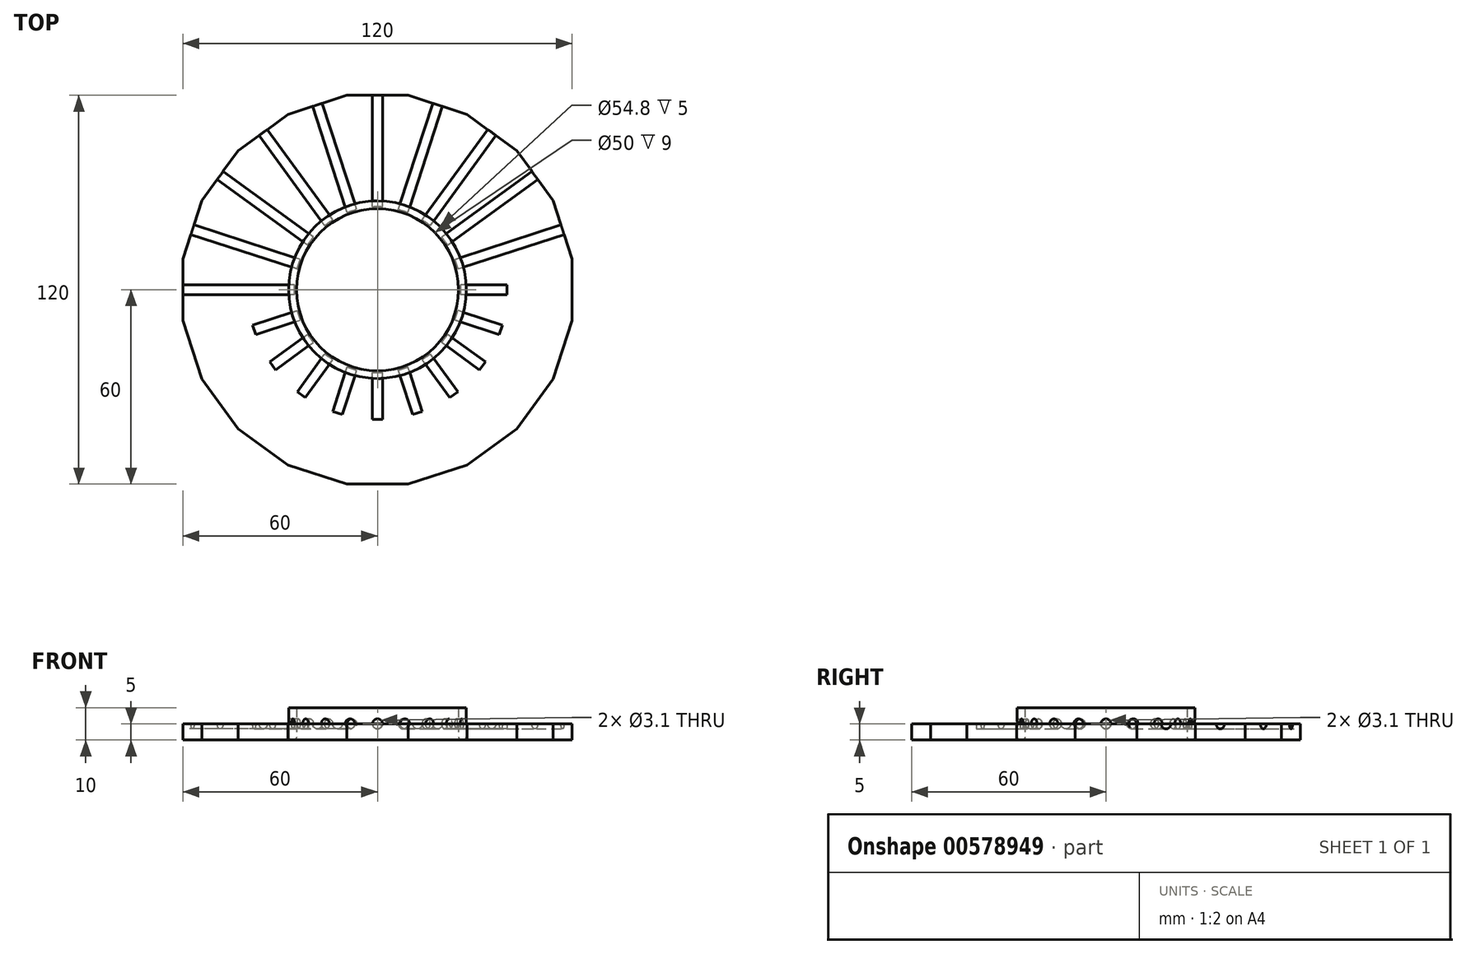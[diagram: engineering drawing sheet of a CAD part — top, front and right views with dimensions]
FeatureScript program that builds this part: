
annotation { "Feature Type Name" : "Feature", "Feature Type Description" : "" }
export const myFeature = defineFeature(function(context is Context, id is Id, definition is map)
    precondition{}
    {
        {
            var Q0;
            Q0=qCreatedBy(makeId("Top.planeOp"),FACE);
            var sketch = newSketch(context, id + "F0", { "sketchPlane" : qUnion([Q0])});
            skCircle(sketch, "E0", {"center": v(0, 0) * mm, "radius": 27.4 * mm});
            skCircle(sketch, "E1.0", {"center": v(0, 0) * mm, "radius": 25.6 * mm});
            skCircle(sketch, "E2.cCircle", {"center": v(0, 0) * mm, "radius": 60 * mm, "construction": true});
            skLineSegment(sketch, "E2.0", {"start": v(-60, -9.5) * mm, "end": v(-60, 9.5) * mm});
            skLineSegment(sketch, "E2.1", {"start": v(-60, 9.5) * mm, "end": v(-54.13, 27.58) * mm});
            skLineSegment(sketch, "E2.2", {"start": v(-54.13, 27.58) * mm, "end": v(-42.96, 42.96) * mm});
            skLineSegment(sketch, "E2.3", {"start": v(-42.96, 42.96) * mm, "end": v(-27.58, 54.13) * mm});
            skLineSegment(sketch, "E2.4", {"start": v(-27.58, 54.13) * mm, "end": v(-9.5, 60) * mm});
            skLineSegment(sketch, "E2.5", {"start": v(-9.5, 60) * mm, "end": v(9.5, 60) * mm});
            skLineSegment(sketch, "E2.6", {"start": v(9.5, 60) * mm, "end": v(27.58, 54.13) * mm});
            skLineSegment(sketch, "E2.7", {"start": v(27.58, 54.13) * mm, "end": v(42.96, 42.96) * mm});
            skLineSegment(sketch, "E2.8", {"start": v(42.96, 42.96) * mm, "end": v(54.13, 27.58) * mm});
            skLineSegment(sketch, "E2.9", {"start": v(54.13, 27.58) * mm, "end": v(60, 9.5) * mm});
            skLineSegment(sketch, "E2.10", {"start": v(60, 9.5) * mm, "end": v(60, -9.5) * mm});
            skLineSegment(sketch, "E2.11", {"start": v(60, -9.5) * mm, "end": v(54.13, -27.58) * mm});
            skLineSegment(sketch, "E2.12", {"start": v(54.13, -27.58) * mm, "end": v(42.96, -42.96) * mm});
            skLineSegment(sketch, "E2.13", {"start": v(42.96, -42.96) * mm, "end": v(27.58, -54.13) * mm});
            skLineSegment(sketch, "E2.14", {"start": v(27.58, -54.13) * mm, "end": v(9.5, -60) * mm});
            skLineSegment(sketch, "E2.15", {"start": v(9.5, -60) * mm, "end": v(-9.5, -60) * mm});
            skLineSegment(sketch, "E2.16", {"start": v(-9.5, -60) * mm, "end": v(-27.58, -54.13) * mm});
            skLineSegment(sketch, "E2.17", {"start": v(-27.58, -54.13) * mm, "end": v(-42.96, -42.96) * mm});
            skLineSegment(sketch, "E2.18", {"start": v(-42.96, -42.96) * mm, "end": v(-54.13, -27.58) * mm});
            skLineSegment(sketch, "E2.19", {"start": v(-54.13, -27.58) * mm, "end": v(-60, -9.5) * mm});
            skPoint(sketch, "E2.0.midPoint", {"position": v(-60, 0) * mm});
            skCircle(sketch, "E3.0", {"center": v(0, 0) * mm, "radius": 25 * mm});
            skSolve(sketch);
        }
        {
            var Q0;
            Q0=makeQuery(id+"F0.imprint","IMPRINT",FACE,{"disambiguationData":[TD([[makeQuery(id+"F0.imprint","IMPRINT",EDGE,{"derivedFrom":sQuery(id+"F0.wireOp",EDGE,"E0")}),1.0]])]});
            extrude(context, id + "F1", {"entities" : qUnion([Q0]), "depth" : 10 * mm, "offsetDistance" : 25 * mm});
        }
        {
            var Q0;
            Q0=makeQuery(id+"F0.imprint","IMPRINT",FACE,{"disambiguationData":[TD([[makeQuery(id+"F0.imprint","IMPRINT",EDGE,{"derivedFrom":sQuery(id+"F0.wireOp",EDGE,"E0")}),-1.0]])]});
            extrude(context, id + "F2", {"entities" : qUnion([Q0]), "depth" : 5 * mm, "offsetDistance" : 25 * mm});
        }
        {
            var Q0;
            Q0=makeQuery(id+"F2.opExtrude","SWEPT_FACE",FACE,{"disambiguationData":[OSD([sQuery(id+"F0.wireOp",EDGE,"E2.1")])]});
            var sketch = newSketch(context, id + "F3", { "sketchPlane" : qUnion([Q0])});
            skCircle(sketch, "E4", {"center": v(0, 5) * mm, "radius": 1.55 * mm});
            skSolve(sketch);
        }
        {
            var Q0;
            Q0=makeQuery(id+"F2.opExtrude","SWEPT_FACE",FACE,{"disambiguationData":[OSD([sQuery(id+"F0.wireOp",EDGE,"E2.0")])]});
            var sketch = newSketch(context, id + "F4", { "sketchPlane" : qUnion([Q0])});
            skCircle(sketch, "E5", {"center": v(0, 5) * mm, "radius": 1.55 * mm});
            skSolve(sketch);
        }
        {
            var Q0;
            Q0=makeQuery(id+"F2.opExtrude","SWEPT_FACE",FACE,{"disambiguationData":[OSD([sQuery(id+"F0.wireOp",EDGE,"E2.2")])]});
            var sketch = newSketch(context, id + "F5", { "sketchPlane" : qUnion([Q0])});
            skCircle(sketch, "E6", {"center": v(0, 5) * mm, "radius": 1.55 * mm});
            skSolve(sketch);
        }
        {
            var Q0;
            Q0=makeQuery(id+"F2.opExtrude","SWEPT_FACE",FACE,{"disambiguationData":[OSD([sQuery(id+"F0.wireOp",EDGE,"E2.3")])]});
            var sketch = newSketch(context, id + "F6", { "sketchPlane" : qUnion([Q0])});
            skCircle(sketch, "E7", {"center": v(0, 5) * mm, "radius": 1.55 * mm});
            skSolve(sketch);
        }
        {
            var Q0;
            Q0=makeQuery(id+"F2.opExtrude","SWEPT_FACE",FACE,{"disambiguationData":[OSD([sQuery(id+"F0.wireOp",EDGE,"E2.4")])]});
            var sketch = newSketch(context, id + "F7", { "sketchPlane" : qUnion([Q0])});
            skCircle(sketch, "E8", {"center": v(0, 5) * mm, "radius": 1.55 * mm});
            skSolve(sketch);
        }
        {
            var Q0;
            Q0=makeQuery(id+"F2.opExtrude","SWEPT_FACE",FACE,{"disambiguationData":[OSD([sQuery(id+"F0.wireOp",EDGE,"E2.5")])]});
            var sketch = newSketch(context, id + "F8", { "sketchPlane" : qUnion([Q0])});
            skCircle(sketch, "E9", {"center": v(0, 5) * mm, "radius": 1.55 * mm});
            skSolve(sketch);
        }
        {
            var Q0;
            Q0=makeQuery(id+"F2.opExtrude","SWEPT_FACE",FACE,{"disambiguationData":[OSD([sQuery(id+"F0.wireOp",EDGE,"E2.6")])]});
            var sketch = newSketch(context, id + "F9", { "sketchPlane" : qUnion([Q0])});
            skCircle(sketch, "E10", {"center": v(0, 5) * mm, "radius": 1.55 * mm});
            skSolve(sketch);
        }
        {
            var Q0;
            Q0=makeQuery(id+"F2.opExtrude","SWEPT_FACE",FACE,{"disambiguationData":[OSD([sQuery(id+"F0.wireOp",EDGE,"E2.7")])]});
            var sketch = newSketch(context, id + "F10", { "sketchPlane" : qUnion([Q0])});
            skCircle(sketch, "E11", {"center": v(0, 5) * mm, "radius": 1.55 * mm});
            skSolve(sketch);
        }
        {
            var Q0;
            Q0=makeQuery(id+"F2.opExtrude","SWEPT_FACE",FACE,{"disambiguationData":[OSD([sQuery(id+"F0.wireOp",EDGE,"E2.8")])]});
            var sketch = newSketch(context, id + "F11", { "sketchPlane" : qUnion([Q0])});
            skCircle(sketch, "E12", {"center": v(0, 5) * mm, "radius": 1.55 * mm});
            skSolve(sketch);
        }
        {
            var Q0;
            Q0=makeQuery(id+"F2.opExtrude","SWEPT_FACE",FACE,{"disambiguationData":[OSD([sQuery(id+"F0.wireOp",EDGE,"E2.9")])]});
            var sketch = newSketch(context, id + "F12", { "sketchPlane" : qUnion([Q0])});
            skCircle(sketch, "E13", {"center": v(0, 5) * mm, "radius": 1.55 * mm});
            skSolve(sketch);
        }
        {
            var Q0;
            {var subQ0=sQuery(id+"F4.wireOp",EDGE,"E5");var subQ1=makeQuery(id+"F2.opExtrude","CAP_EDGE",EDGE,{"disambiguationData":[OSD([sQuery(id+"F0.wireOp",EDGE,"E2.0")])],"isStart":false});var subQ2=makeQuery(id+"F4.imprint","INTERSECT",VERTEX,{"disambiguationData":[OD(0.0)],"derivedFrom":[subQ1,subQ0]});Q0=makeQuery(id+"F4.imprint","IMPRINT",FACE,{"disambiguationData":[TD([[makeQuery(id+"F4.imprint","IMPRINT",EDGE,{"disambiguationData":[TD([[subQ2,1.0]])],"derivedFrom":subQ0}),1.0]])]});}
            var Q1;
            {var subQ0=sQuery(id+"F4.wireOp",EDGE,"E5");var subQ1=makeQuery(id+"F2.opExtrude","CAP_EDGE",EDGE,{"disambiguationData":[OSD([sQuery(id+"F0.wireOp",EDGE,"E2.0")])],"isStart":false});var subQ2=makeQuery(id+"F4.imprint","INTERSECT",VERTEX,{"disambiguationData":[OD(0.0)],"derivedFrom":[subQ1,subQ0]});Q1=makeQuery(id+"F4.imprint","IMPRINT",FACE,{"disambiguationData":[TD([[makeQuery(id+"F4.imprint","IMPRINT",EDGE,{"disambiguationData":[TD([[subQ2,-1.0]])],"derivedFrom":subQ0}),1.0]])]});}
            extrude(context, id + "F13", {"entities" : qUnion([Q0, Q1]), "operationType" : NewBodyOperationType.REMOVE, "oppositeDirection" : true, "depth" : 100 * mm, "offsetDistance" : 25 * mm});
        }
        {
            var Q0;
            {var subQ0=sQuery(id+"F3.wireOp",EDGE,"E4");var subQ1=makeQuery(id+"F2.opExtrude","CAP_EDGE",EDGE,{"disambiguationData":[OSD([sQuery(id+"F0.wireOp",EDGE,"E2.1")])],"isStart":false});var subQ2=makeQuery(id+"F3.imprint","INTERSECT",VERTEX,{"disambiguationData":[OD(0.0)],"derivedFrom":[subQ1,subQ0]});Q0=makeQuery(id+"F3.imprint","IMPRINT",FACE,{"disambiguationData":[TD([[makeQuery(id+"F3.imprint","IMPRINT",EDGE,{"disambiguationData":[TD([[subQ2,-1.0]])],"derivedFrom":subQ0}),1.0]])]});}
            var Q1;
            {var subQ0=sQuery(id+"F3.wireOp",EDGE,"E4");var subQ1=makeQuery(id+"F2.opExtrude","CAP_EDGE",EDGE,{"disambiguationData":[OSD([sQuery(id+"F0.wireOp",EDGE,"E2.1")])],"isStart":false});var subQ2=makeQuery(id+"F3.imprint","INTERSECT",VERTEX,{"disambiguationData":[OD(0.0)],"derivedFrom":[subQ1,subQ0]});Q1=makeQuery(id+"F3.imprint","IMPRINT",FACE,{"disambiguationData":[TD([[makeQuery(id+"F3.imprint","IMPRINT",EDGE,{"disambiguationData":[TD([[subQ2,1.0]])],"derivedFrom":subQ0}),1.0]])]});}
            extrude(context, id + "F14", {"entities" : qUnion([Q0, Q1]), "operationType" : NewBodyOperationType.REMOVE, "oppositeDirection" : true, "depth" : 100 * mm, "offsetDistance" : 25 * mm});
        }
        {
            var Q0;
            {var subQ0=sQuery(id+"F5.wireOp",EDGE,"E6");var subQ1=makeQuery(id+"F2.opExtrude","CAP_EDGE",EDGE,{"disambiguationData":[OSD([sQuery(id+"F0.wireOp",EDGE,"E2.2")])],"isStart":false});var subQ2=makeQuery(id+"F5.imprint","INTERSECT",VERTEX,{"disambiguationData":[OD(0.0)],"derivedFrom":[subQ1,subQ0]});Q0=makeQuery(id+"F5.imprint","IMPRINT",FACE,{"disambiguationData":[TD([[makeQuery(id+"F5.imprint","IMPRINT",EDGE,{"disambiguationData":[TD([[subQ2,1.0]])],"derivedFrom":subQ0}),1.0]])]});}
            var Q1;
            {var subQ0=sQuery(id+"F5.wireOp",EDGE,"E6");var subQ1=makeQuery(id+"F2.opExtrude","CAP_EDGE",EDGE,{"disambiguationData":[OSD([sQuery(id+"F0.wireOp",EDGE,"E2.2")])],"isStart":false});var subQ2=makeQuery(id+"F5.imprint","INTERSECT",VERTEX,{"disambiguationData":[OD(0.0)],"derivedFrom":[subQ1,subQ0]});Q1=makeQuery(id+"F5.imprint","IMPRINT",FACE,{"disambiguationData":[TD([[makeQuery(id+"F5.imprint","IMPRINT",EDGE,{"disambiguationData":[TD([[subQ2,-1.0]])],"derivedFrom":subQ0}),1.0]])]});}
            extrude(context, id + "F15", {"entities" : qUnion([Q0, Q1]), "operationType" : NewBodyOperationType.REMOVE, "oppositeDirection" : true, "depth" : 100 * mm, "offsetDistance" : 25 * mm});
        }
        {
            var Q0;
            {var subQ0=sQuery(id+"F6.wireOp",EDGE,"E7");var subQ1=makeQuery(id+"F2.opExtrude","CAP_EDGE",EDGE,{"disambiguationData":[OSD([sQuery(id+"F0.wireOp",EDGE,"E2.3")])],"isStart":false});var subQ2=makeQuery(id+"F6.imprint","INTERSECT",VERTEX,{"disambiguationData":[OD(0.0)],"derivedFrom":[subQ1,subQ0]});Q0=makeQuery(id+"F6.imprint","IMPRINT",FACE,{"disambiguationData":[TD([[makeQuery(id+"F6.imprint","IMPRINT",EDGE,{"disambiguationData":[TD([[subQ2,-1.0]])],"derivedFrom":subQ0}),1.0]])]});}
            var Q1;
            {var subQ0=sQuery(id+"F6.wireOp",EDGE,"E7");var subQ1=makeQuery(id+"F2.opExtrude","CAP_EDGE",EDGE,{"disambiguationData":[OSD([sQuery(id+"F0.wireOp",EDGE,"E2.3")])],"isStart":false});var subQ2=makeQuery(id+"F6.imprint","INTERSECT",VERTEX,{"disambiguationData":[OD(0.0)],"derivedFrom":[subQ1,subQ0]});Q1=makeQuery(id+"F6.imprint","IMPRINT",FACE,{"disambiguationData":[TD([[makeQuery(id+"F6.imprint","IMPRINT",EDGE,{"disambiguationData":[TD([[subQ2,1.0]])],"derivedFrom":subQ0}),1.0]])]});}
            extrude(context, id + "F16", {"entities" : qUnion([Q0, Q1]), "operationType" : NewBodyOperationType.REMOVE, "oppositeDirection" : true, "depth" : 100 * mm, "offsetDistance" : 25 * mm});
        }
        {
            var Q0;
            {var subQ0=sQuery(id+"F7.wireOp",EDGE,"E8");var subQ1=makeQuery(id+"F2.opExtrude","CAP_EDGE",EDGE,{"disambiguationData":[OSD([sQuery(id+"F0.wireOp",EDGE,"E2.4")])],"isStart":false});var subQ2=makeQuery(id+"F7.imprint","INTERSECT",VERTEX,{"disambiguationData":[OD(0.0)],"derivedFrom":[subQ1,subQ0]});Q0=makeQuery(id+"F7.imprint","IMPRINT",FACE,{"disambiguationData":[TD([[makeQuery(id+"F7.imprint","IMPRINT",EDGE,{"disambiguationData":[TD([[subQ2,1.0]])],"derivedFrom":subQ0}),1.0]])]});}
            var Q1;
            {var subQ0=sQuery(id+"F7.wireOp",EDGE,"E8");var subQ1=makeQuery(id+"F2.opExtrude","CAP_EDGE",EDGE,{"disambiguationData":[OSD([sQuery(id+"F0.wireOp",EDGE,"E2.4")])],"isStart":false});var subQ2=makeQuery(id+"F7.imprint","INTERSECT",VERTEX,{"disambiguationData":[OD(0.0)],"derivedFrom":[subQ1,subQ0]});Q1=makeQuery(id+"F7.imprint","IMPRINT",FACE,{"disambiguationData":[TD([[makeQuery(id+"F7.imprint","IMPRINT",EDGE,{"disambiguationData":[TD([[subQ2,-1.0]])],"derivedFrom":subQ0}),1.0]])]});}
            extrude(context, id + "F17", {"entities" : qUnion([Q0, Q1]), "operationType" : NewBodyOperationType.REMOVE, "oppositeDirection" : true, "depth" : 100 * mm, "offsetDistance" : 25 * mm});
        }
        {
            var Q0;
            {var subQ0=sQuery(id+"F8.wireOp",EDGE,"E9");var subQ1=makeQuery(id+"F2.opExtrude","CAP_EDGE",EDGE,{"disambiguationData":[OSD([sQuery(id+"F0.wireOp",EDGE,"E2.5")])],"isStart":false});var subQ2=makeQuery(id+"F8.imprint","INTERSECT",VERTEX,{"disambiguationData":[OD(0.0)],"derivedFrom":[subQ1,subQ0]});Q0=makeQuery(id+"F8.imprint","IMPRINT",FACE,{"disambiguationData":[TD([[makeQuery(id+"F8.imprint","IMPRINT",EDGE,{"disambiguationData":[TD([[subQ2,1.0]])],"derivedFrom":subQ0}),1.0]])]});}
            var Q1;
            {var subQ0=sQuery(id+"F8.wireOp",EDGE,"E9");var subQ1=makeQuery(id+"F2.opExtrude","CAP_EDGE",EDGE,{"disambiguationData":[OSD([sQuery(id+"F0.wireOp",EDGE,"E2.5")])],"isStart":false});var subQ2=makeQuery(id+"F8.imprint","INTERSECT",VERTEX,{"disambiguationData":[OD(0.0)],"derivedFrom":[subQ1,subQ0]});Q1=makeQuery(id+"F8.imprint","IMPRINT",FACE,{"disambiguationData":[TD([[makeQuery(id+"F8.imprint","IMPRINT",EDGE,{"disambiguationData":[TD([[subQ2,-1.0]])],"derivedFrom":subQ0}),1.0]])]});}
            extrude(context, id + "F18", {"entities" : qUnion([Q0, Q1]), "operationType" : NewBodyOperationType.REMOVE, "oppositeDirection" : true, "depth" : 100 * mm, "offsetDistance" : 25 * mm});
        }
        {
            var Q0;
            {var subQ0=sQuery(id+"F9.wireOp",EDGE,"E10");var subQ1=makeQuery(id+"F2.opExtrude","CAP_EDGE",EDGE,{"disambiguationData":[OSD([sQuery(id+"F0.wireOp",EDGE,"E2.6")])],"isStart":false});var subQ2=makeQuery(id+"F9.imprint","INTERSECT",VERTEX,{"disambiguationData":[OD(0.0)],"derivedFrom":[subQ1,subQ0]});Q0=makeQuery(id+"F9.imprint","IMPRINT",FACE,{"disambiguationData":[TD([[makeQuery(id+"F9.imprint","IMPRINT",EDGE,{"disambiguationData":[TD([[subQ2,-1.0]])],"derivedFrom":subQ0}),1.0]])]});}
            var Q1;
            {var subQ0=sQuery(id+"F9.wireOp",EDGE,"E10");var subQ1=makeQuery(id+"F2.opExtrude","CAP_EDGE",EDGE,{"disambiguationData":[OSD([sQuery(id+"F0.wireOp",EDGE,"E2.6")])],"isStart":false});var subQ2=makeQuery(id+"F9.imprint","INTERSECT",VERTEX,{"disambiguationData":[OD(0.0)],"derivedFrom":[subQ1,subQ0]});Q1=makeQuery(id+"F9.imprint","IMPRINT",FACE,{"disambiguationData":[TD([[makeQuery(id+"F9.imprint","IMPRINT",EDGE,{"disambiguationData":[TD([[subQ2,1.0]])],"derivedFrom":subQ0}),1.0]])]});}
            extrude(context, id + "F19", {"entities" : qUnion([Q0, Q1]), "operationType" : NewBodyOperationType.REMOVE, "oppositeDirection" : true, "depth" : 100 * mm, "offsetDistance" : 25 * mm});
        }
        {
            var Q0;
            {var subQ0=sQuery(id+"F10.wireOp",EDGE,"E11");var subQ1=makeQuery(id+"F2.opExtrude","CAP_EDGE",EDGE,{"disambiguationData":[OSD([sQuery(id+"F0.wireOp",EDGE,"E2.7")])],"isStart":false});var subQ2=makeQuery(id+"F10.imprint","INTERSECT",VERTEX,{"disambiguationData":[OD(0.0)],"derivedFrom":[subQ1,subQ0]});Q0=makeQuery(id+"F10.imprint","IMPRINT",FACE,{"disambiguationData":[TD([[makeQuery(id+"F10.imprint","IMPRINT",EDGE,{"disambiguationData":[TD([[subQ2,-1.0]])],"derivedFrom":subQ0}),1.0]])]});}
            var Q1;
            {var subQ0=sQuery(id+"F10.wireOp",EDGE,"E11");var subQ1=makeQuery(id+"F2.opExtrude","CAP_EDGE",EDGE,{"disambiguationData":[OSD([sQuery(id+"F0.wireOp",EDGE,"E2.7")])],"isStart":false});var subQ2=makeQuery(id+"F10.imprint","INTERSECT",VERTEX,{"disambiguationData":[OD(0.0)],"derivedFrom":[subQ1,subQ0]});Q1=makeQuery(id+"F10.imprint","IMPRINT",FACE,{"disambiguationData":[TD([[makeQuery(id+"F10.imprint","IMPRINT",EDGE,{"disambiguationData":[TD([[subQ2,1.0]])],"derivedFrom":subQ0}),1.0]])]});}
            extrude(context, id + "F20", {"entities" : qUnion([Q0, Q1]), "operationType" : NewBodyOperationType.REMOVE, "oppositeDirection" : true, "depth" : 100 * mm, "offsetDistance" : 25 * mm});
        }
        {
            var Q0;
            {var subQ0=sQuery(id+"F11.wireOp",EDGE,"E12");var subQ1=makeQuery(id+"F2.opExtrude","CAP_EDGE",EDGE,{"disambiguationData":[OSD([sQuery(id+"F0.wireOp",EDGE,"E2.8")])],"isStart":false});var subQ2=makeQuery(id+"F11.imprint","INTERSECT",VERTEX,{"disambiguationData":[OD(0.0)],"derivedFrom":[subQ1,subQ0]});Q0=makeQuery(id+"F11.imprint","IMPRINT",FACE,{"disambiguationData":[TD([[makeQuery(id+"F11.imprint","IMPRINT",EDGE,{"disambiguationData":[TD([[subQ2,-1.0]])],"derivedFrom":subQ0}),1.0]])]});}
            var Q1;
            {var subQ0=sQuery(id+"F11.wireOp",EDGE,"E12");var subQ1=makeQuery(id+"F2.opExtrude","CAP_EDGE",EDGE,{"disambiguationData":[OSD([sQuery(id+"F0.wireOp",EDGE,"E2.8")])],"isStart":false});var subQ2=makeQuery(id+"F11.imprint","INTERSECT",VERTEX,{"disambiguationData":[OD(0.0)],"derivedFrom":[subQ1,subQ0]});Q1=makeQuery(id+"F11.imprint","IMPRINT",FACE,{"disambiguationData":[TD([[makeQuery(id+"F11.imprint","IMPRINT",EDGE,{"disambiguationData":[TD([[subQ2,1.0]])],"derivedFrom":subQ0}),1.0]])]});}
            extrude(context, id + "F21", {"entities" : qUnion([Q0, Q1]), "operationType" : NewBodyOperationType.REMOVE, "oppositeDirection" : true, "depth" : 100 * mm, "offsetDistance" : 25 * mm});
        }
        {
            var Q0;
            {var subQ0=sQuery(id+"F12.wireOp",EDGE,"E13");var subQ1=makeQuery(id+"F2.opExtrude","CAP_EDGE",EDGE,{"disambiguationData":[OSD([sQuery(id+"F0.wireOp",EDGE,"E2.9")])],"isStart":false});var subQ2=makeQuery(id+"F12.imprint","INTERSECT",VERTEX,{"disambiguationData":[OD(0.0)],"derivedFrom":[subQ1,subQ0]});Q0=makeQuery(id+"F12.imprint","IMPRINT",FACE,{"disambiguationData":[TD([[makeQuery(id+"F12.imprint","IMPRINT",EDGE,{"disambiguationData":[TD([[subQ2,-1.0]])],"derivedFrom":subQ0}),1.0]])]});}
            var Q1;
            {var subQ0=sQuery(id+"F12.wireOp",EDGE,"E13");var subQ1=makeQuery(id+"F2.opExtrude","CAP_EDGE",EDGE,{"disambiguationData":[OSD([sQuery(id+"F0.wireOp",EDGE,"E2.9")])],"isStart":false});var subQ2=makeQuery(id+"F12.imprint","INTERSECT",VERTEX,{"disambiguationData":[OD(0.0)],"derivedFrom":[subQ1,subQ0]});Q1=makeQuery(id+"F12.imprint","IMPRINT",FACE,{"disambiguationData":[TD([[makeQuery(id+"F12.imprint","IMPRINT",EDGE,{"disambiguationData":[TD([[subQ2,1.0]])],"derivedFrom":subQ0}),1.0]])]});}
            extrude(context, id + "F22", {"entities" : qUnion([Q0, Q1]), "operationType" : NewBodyOperationType.REMOVE, "oppositeDirection" : true, "depth" : 100 * mm, "offsetDistance" : 25 * mm});
        }
        {
            var Q0;
            Q0=makeQuery(id+"F0.imprint","IMPRINT",FACE,{"disambiguationData":[TD([[makeQuery(id+"F0.imprint","IMPRINT",EDGE,{"derivedFrom":sQuery(id+"F0.wireOp",EDGE,"E1.0")}),1.0]])]});
            extrude(context, id + "F23", {"entities" : qUnion([Q0]), "operationType" : NewBodyOperationType.ADD, "depth" : 10 * mm, "offsetDistance" : 25 * mm});
        }
        {
            var Q0;
            Q0=makeQuery(id+"F1.opExtrude","CAP_EDGE",EDGE,{"disambiguationData":[OSD([sQuery(id+"F0.wireOp",EDGE,"E0")])],"isStart":true});
            var Q1;
            Q1=makeQuery(id+"F23.opExtrude","CAP_EDGE",EDGE,{"disambiguationData":[OSD([sQuery(id+"F0.wireOp",EDGE,"E3.0")])],"isStart":true});
            fillet(context, id + "F24", {"entities" : qUnion([Q0, Q1]), "radius" : 1 * mm, "tangentPropagation" : true, "allowEdgeOverflow" : false});
        }
    });
